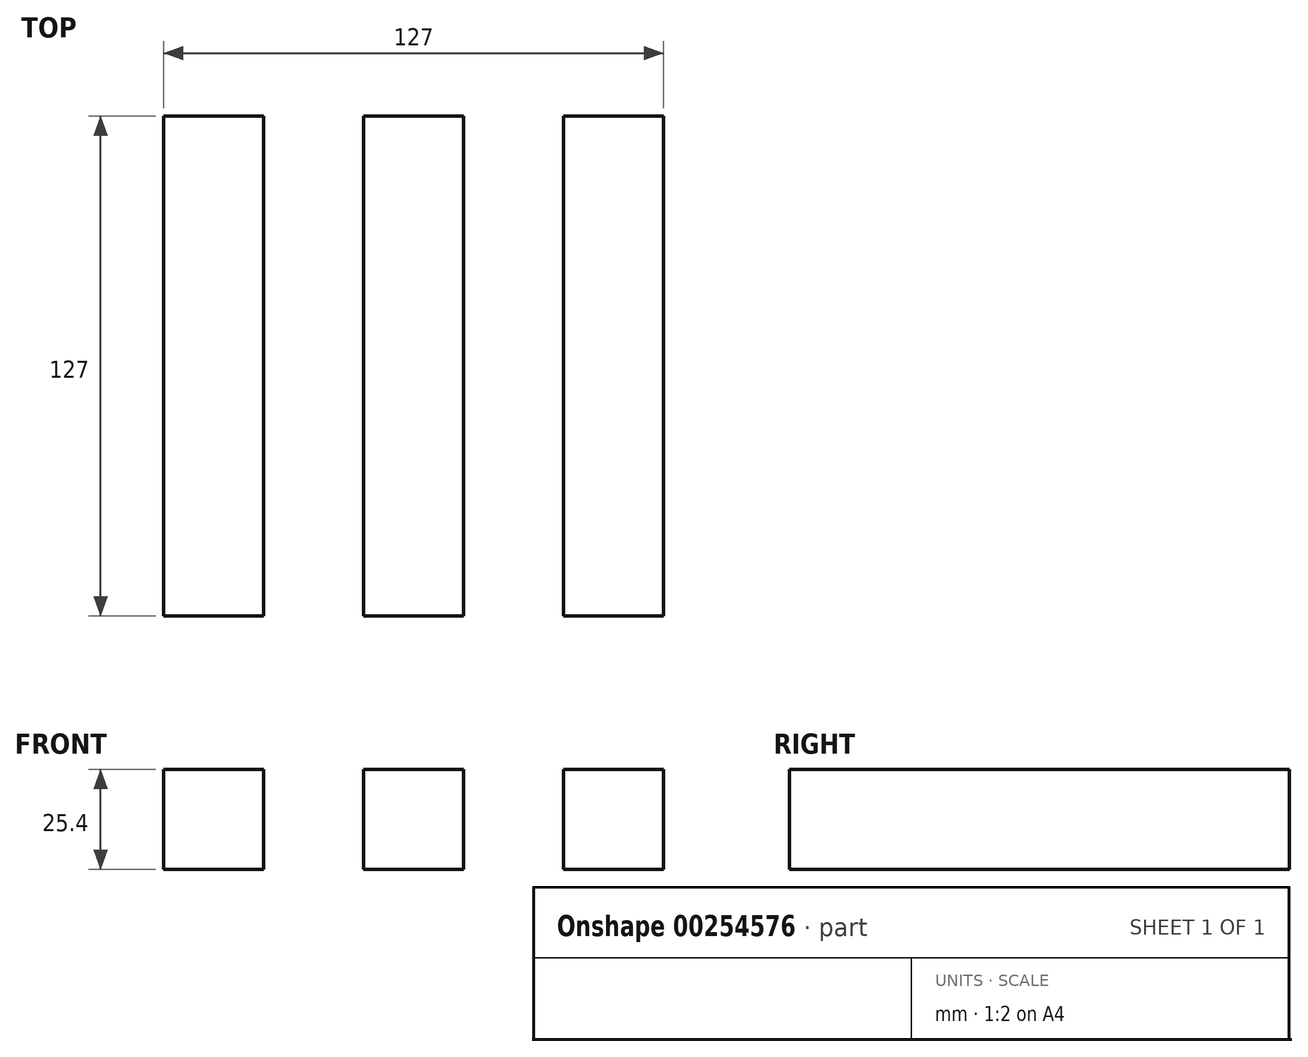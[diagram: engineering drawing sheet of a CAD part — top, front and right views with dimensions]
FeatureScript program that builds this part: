
annotation { "Feature Type Name" : "Feature", "Feature Type Description" : "" }
export const myFeature = defineFeature(function(context is Context, id is Id, definition is map)
    precondition{}
    {
        {
            var Q0;
            Q0=qCreatedBy(makeId("Front.planeOp"),FACE);
            var sketch = newSketch(context, id + "F0", { "sketchPlane" : qUnion([Q0])});
            skLineSegment(sketch, "E0.bottom", {"start": v(-38.1, -12.7) * mm, "end": v(-63.5, -12.7) * mm});
            skLineSegment(sketch, "E0.top", {"start": v(-38.1, 12.7) * mm, "end": v(-63.5, 12.7) * mm});
            skLineSegment(sketch, "E0.left", {"start": v(-38.1, -12.7) * mm, "end": v(-38.1, 12.7) * mm});
            skLineSegment(sketch, "E0.right", {"start": v(-63.5, -12.7) * mm, "end": v(-63.5, 12.7) * mm});
            skPoint(sketch, "E0.middle", {"position": v(-50.8, 0) * mm});
            skLineSegment(sketch, "E1.bottom", {"start": v(12.7, -12.7) * mm, "end": v(-12.7, -12.7) * mm});
            skLineSegment(sketch, "E1.top", {"start": v(12.7, 12.7) * mm, "end": v(-12.7, 12.7) * mm});
            skLineSegment(sketch, "E1.left", {"start": v(12.7, -12.7) * mm, "end": v(12.7, 12.7) * mm});
            skLineSegment(sketch, "E1.right", {"start": v(-12.7, -12.7) * mm, "end": v(-12.7, 12.7) * mm});
            skPoint(sketch, "E1.middle", {"position": v(0, 0) * mm});
            skLineSegment(sketch, "E2.bottom", {"start": v(63.5, -12.7) * mm, "end": v(38.1, -12.7) * mm});
            skLineSegment(sketch, "E2.top", {"start": v(63.5, 12.7) * mm, "end": v(38.1, 12.7) * mm});
            skLineSegment(sketch, "E2.left", {"start": v(63.5, -12.7) * mm, "end": v(63.5, 12.7) * mm});
            skLineSegment(sketch, "E2.right", {"start": v(38.1, -12.7) * mm, "end": v(38.1, 12.7) * mm});
            skPoint(sketch, "E2.middle", {"position": v(50.8, 0) * mm});
            skLineSegment(sketch, "E3", {"start": v(-50.8, 0) * mm, "end": v(0, 0) * mm});
            skLineSegment(sketch, "E4", {"start": v(0, 0) * mm, "end": v(50.8, 0) * mm});
            skSolve(sketch);
        }
        {
            var Q0;
            {var subQ1=sQuery(id+"F0.wireOp",EDGE,"E2.bottom");Q0=makeQuery(id+"F0.imprint","IMPRINT",FACE,{"disambiguationData":[TD([[makeQuery(id+"F0.imprint","IMPRINT",EDGE,{"derivedFrom":subQ1}),-1.0]])]});}
            var Q1;
            {var subQ5=sQuery(id+"F0.wireOp",EDGE,"E1.bottom");Q1=makeQuery(id+"F0.imprint","IMPRINT",FACE,{"disambiguationData":[TD([[makeQuery(id+"F0.imprint","IMPRINT",EDGE,{"derivedFrom":subQ5}),-1.0]])]});}
            var Q2;
            {var subQ5=sQuery(id+"F0.wireOp",EDGE,"E1.top");Q2=makeQuery(id+"F0.imprint","IMPRINT",FACE,{"disambiguationData":[TD([[makeQuery(id+"F0.imprint","IMPRINT",EDGE,{"derivedFrom":subQ5}),1.0]])]});}
            var Q3;
            {var subQ3=sQuery(id+"F0.wireOp",EDGE,"E0.bottom");Q3=makeQuery(id+"F0.imprint","IMPRINT",FACE,{"disambiguationData":[TD([[makeQuery(id+"F0.imprint","IMPRINT",EDGE,{"derivedFrom":subQ3}),-1.0]])]});}
            extrude(context, id + "F1", {"entities" : qUnion([Q0, Q1, Q2, Q3]), "endBound" : BoundingType.SYMMETRIC, "depth" : 127 * mm});
        }
    });
